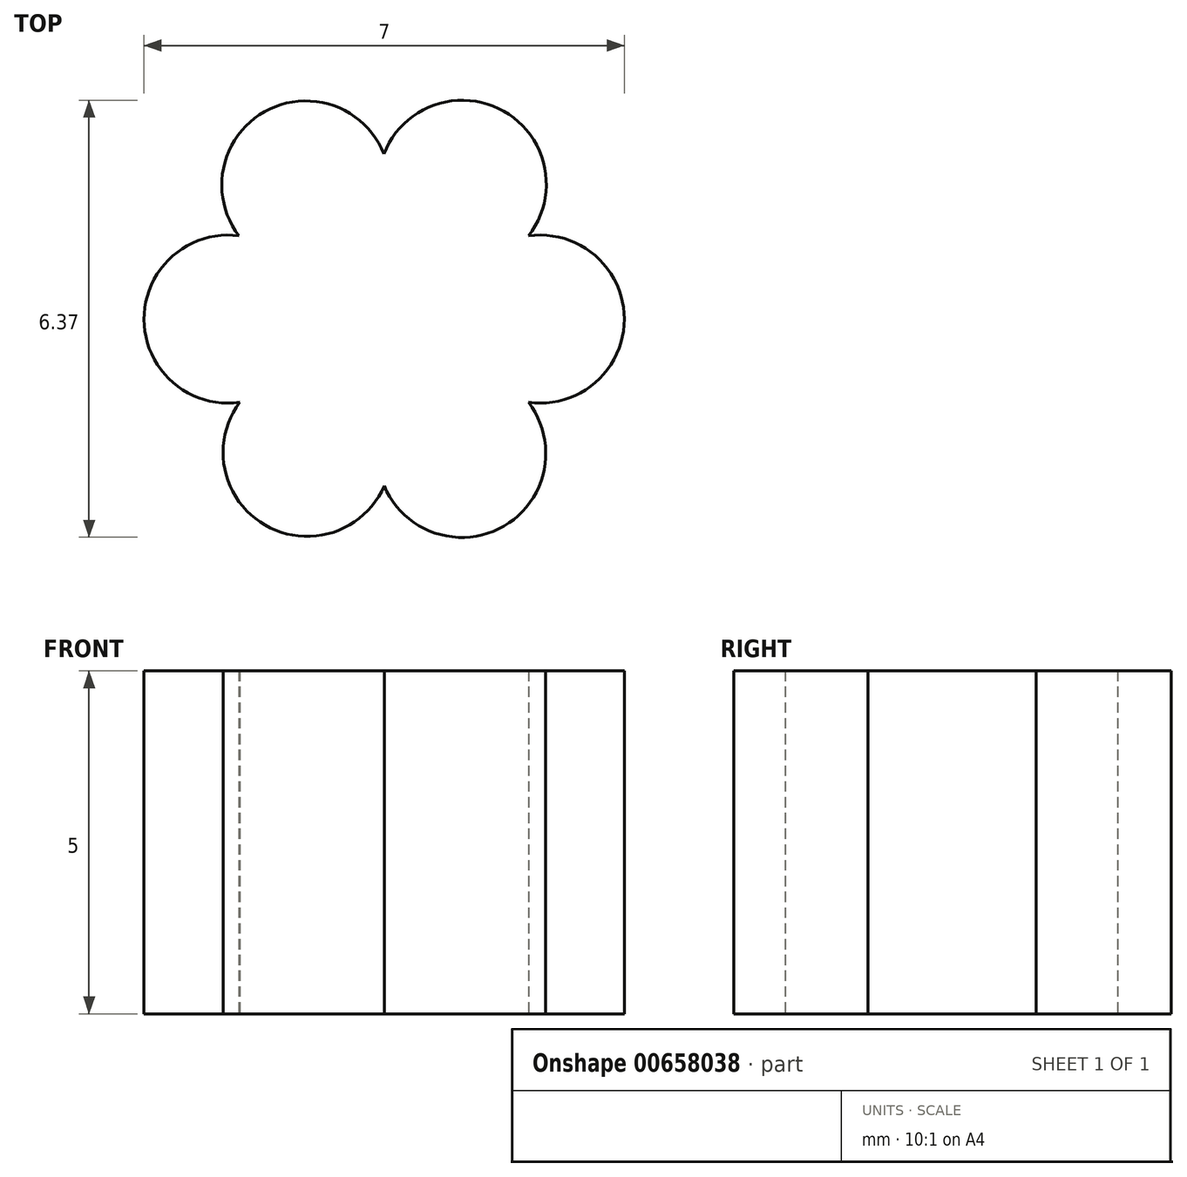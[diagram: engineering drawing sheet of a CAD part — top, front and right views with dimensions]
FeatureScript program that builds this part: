
annotation { "Feature Type Name" : "Feature", "Feature Type Description" : "" }
export const myFeature = defineFeature(function(context is Context, id is Id, definition is map)
    precondition{}
    {
        {
            var Q0;
            Q0=qCreatedBy(makeId("Top.planeOp"),FACE);
            var sketch = newSketch(context, id + "F0", { "sketchPlane" : qUnion([Q0])});
            skCircle(sketch, "E0", {"center": v(0, 0) * mm, "radius": 3.5 * mm});
            skCircle(sketch, "E1", {"center": v(-1.14, 1.96) * mm, "radius": 1.23 * mm});
            skCircle(sketch, "E2", {"center": v(-2.27, 0) * mm, "radius": 1.23 * mm});
            skCircle(sketch, "E3", {"center": v(-1.12, -1.94) * mm, "radius": 1.23 * mm});
            skCircle(sketch, "E4", {"center": v(1.13, -1.96) * mm, "radius": 1.23 * mm});
            skCircle(sketch, "E5", {"center": v(2.27, 0) * mm, "radius": 1.23 * mm});
            skCircle(sketch, "E6", {"center": v(1.14, 1.97) * mm, "radius": 1.23 * mm});
            skSolve(sketch);
        }
        {
            var Q0;
            {var subQ0=sQuery(id+"F0.wireOp",EDGE,"E2");var subQ1=sQuery(id+"F0.wireOp",EDGE,"E1");var subQ2=makeQuery(id+"F0.imprint","INTERSECT",VERTEX,{"disambiguationData":[OD(0.0)],"derivedFrom":[subQ1,subQ0]});Q0=makeQuery(id+"F0.imprint","IMPRINT",FACE,{"disambiguationData":[TD([[makeQuery(id+"F0.imprint","IMPRINT",EDGE,{"disambiguationData":[TD([[subQ2,1.0]])],"derivedFrom":subQ1}),1.0]])]});}
            var Q1;
            {var subQ0=sQuery(id+"F0.wireOp",EDGE,"E2");var subQ1=sQuery(id+"F0.wireOp",EDGE,"E1");var subQ6=makeQuery(id+"F0.imprint","INTERSECT",VERTEX,{"disambiguationData":[OD(0.0)],"derivedFrom":[subQ1,subQ0]});Q1=makeQuery(id+"F0.imprint","IMPRINT",FACE,{"disambiguationData":[TD([[makeQuery(id+"F0.imprint","IMPRINT",EDGE,{"disambiguationData":[TD([[subQ6,-1.0]])],"derivedFrom":subQ1}),-1.0]])]});}
            var Q2;
            {var subQ0=sQuery(id+"F0.wireOp",EDGE,"E2");var subQ1=sQuery(id+"F0.wireOp",EDGE,"E1");var subQ2=makeQuery(id+"F0.imprint","INTERSECT",VERTEX,{"disambiguationData":[OD(0.0)],"derivedFrom":[subQ1,subQ0]});Q2=makeQuery(id+"F0.imprint","IMPRINT",FACE,{"disambiguationData":[TD([[makeQuery(id+"F0.imprint","IMPRINT",EDGE,{"disambiguationData":[TD([[subQ2,-1.0]])],"derivedFrom":subQ1}),1.0]])]});}
            var Q3;
            {var subQ0=sQuery(id+"F0.wireOp",EDGE,"E3");var subQ1=sQuery(id+"F0.wireOp",EDGE,"E2");var subQ2=makeQuery(id+"F0.imprint","INTERSECT",VERTEX,{"disambiguationData":[OD(0.0)],"derivedFrom":[subQ1,subQ0]});Q3=makeQuery(id+"F0.imprint","IMPRINT",FACE,{"disambiguationData":[TD([[makeQuery(id+"F0.imprint","IMPRINT",EDGE,{"disambiguationData":[TD([[subQ2,-1.0]])],"derivedFrom":subQ1}),1.0]])]});}
            var Q4;
            {var subQ0=sQuery(id+"F0.wireOp",EDGE,"E3");var subQ1=sQuery(id+"F0.wireOp",EDGE,"E2");var subQ2=makeQuery(id+"F0.imprint","INTERSECT",VERTEX,{"disambiguationData":[OD(0.0)],"derivedFrom":[subQ1,subQ0]});Q4=makeQuery(id+"F0.imprint","IMPRINT",FACE,{"disambiguationData":[TD([[makeQuery(id+"F0.imprint","IMPRINT",EDGE,{"disambiguationData":[TD([[subQ2,-1.0]])],"derivedFrom":subQ1}),-1.0]])]});}
            var Q5;
            {var subQ0=sQuery(id+"F0.wireOp",EDGE,"E4");var subQ1=sQuery(id+"F0.wireOp",EDGE,"E3");var subQ2=makeQuery(id+"F0.imprint","INTERSECT",VERTEX,{"disambiguationData":[OD(0.0)],"derivedFrom":[subQ1,subQ0]});Q5=makeQuery(id+"F0.imprint","IMPRINT",FACE,{"disambiguationData":[TD([[makeQuery(id+"F0.imprint","IMPRINT",EDGE,{"disambiguationData":[TD([[subQ2,1.0]])],"derivedFrom":subQ1}),-1.0]])]});}
            var Q6;
            {var subQ0=sQuery(id+"F0.wireOp",EDGE,"E5");var subQ2=sQuery(id+"F0.wireOp",EDGE,"E4");var subQ4=makeQuery(id+"F0.imprint","INTERSECT",VERTEX,{"disambiguationData":[OD(0.0)],"derivedFrom":[subQ2,subQ0]});Q6=makeQuery(id+"F0.imprint","IMPRINT",FACE,{"disambiguationData":[TD([[makeQuery(id+"F0.imprint","IMPRINT",EDGE,{"disambiguationData":[TD([[subQ4,1.0]])],"derivedFrom":subQ2}),-1.0]])]});}
            var Q7;
            {var subQ0=sQuery(id+"F0.wireOp",EDGE,"E6");var subQ1=sQuery(id+"F0.wireOp",EDGE,"E1");var subQ2=makeQuery(id+"F0.imprint","INTERSECT",VERTEX,{"disambiguationData":[OD(0.0)],"derivedFrom":[subQ1,subQ0]});Q7=makeQuery(id+"F0.imprint","IMPRINT",FACE,{"disambiguationData":[TD([[makeQuery(id+"F0.imprint","IMPRINT",EDGE,{"disambiguationData":[TD([[subQ2,1.0]])],"derivedFrom":subQ1}),-1.0]])]});}
            var Q8;
            {var subQ0=sQuery(id+"F0.wireOp",EDGE,"E6");var subQ1=sQuery(id+"F0.wireOp",EDGE,"E1");var subQ2=makeQuery(id+"F0.imprint","INTERSECT",VERTEX,{"disambiguationData":[OD(0.0)],"derivedFrom":[subQ1,subQ0]});Q8=makeQuery(id+"F0.imprint","IMPRINT",FACE,{"disambiguationData":[TD([[makeQuery(id+"F0.imprint","IMPRINT",EDGE,{"disambiguationData":[TD([[subQ2,1.0]])],"derivedFrom":subQ1}),1.0]])]});}
            var Q9;
            {var subQ0=sQuery(id+"F0.wireOp",EDGE,"E6");var subQ1=sQuery(id+"F0.wireOp",EDGE,"E5");var subQ2=makeQuery(id+"F0.imprint","INTERSECT",VERTEX,{"disambiguationData":[OD(0.0)],"derivedFrom":[subQ1,subQ0]});Q9=makeQuery(id+"F0.imprint","IMPRINT",FACE,{"disambiguationData":[TD([[makeQuery(id+"F0.imprint","IMPRINT",EDGE,{"disambiguationData":[TD([[subQ2,-1.0]])],"derivedFrom":subQ1}),1.0]])]});}
            var Q10;
            {var subQ0=sQuery(id+"F0.wireOp",EDGE,"E5");var subQ1=sQuery(id+"F0.wireOp",EDGE,"E4");var subQ2=makeQuery(id+"F0.imprint","INTERSECT",VERTEX,{"disambiguationData":[OD(0.0)],"derivedFrom":[subQ1,subQ0]});Q10=makeQuery(id+"F0.imprint","IMPRINT",FACE,{"disambiguationData":[TD([[makeQuery(id+"F0.imprint","IMPRINT",EDGE,{"disambiguationData":[TD([[subQ2,1.0]])],"derivedFrom":subQ1}),1.0]])]});}
            var Q11;
            {var subQ0=sQuery(id+"F0.wireOp",EDGE,"E4");var subQ1=sQuery(id+"F0.wireOp",EDGE,"E3");var subQ2=makeQuery(id+"F0.imprint","INTERSECT",VERTEX,{"disambiguationData":[OD(0.0)],"derivedFrom":[subQ1,subQ0]});Q11=makeQuery(id+"F0.imprint","IMPRINT",FACE,{"disambiguationData":[TD([[makeQuery(id+"F0.imprint","IMPRINT",EDGE,{"disambiguationData":[TD([[subQ2,1.0]])],"derivedFrom":subQ1}),1.0]])]});}
            var Q12;
            {var subQ5=sQuery(id+"F0.wireOp",EDGE,"E2");var subQ7=sQuery(id+"F0.wireOp",EDGE,"E1");var subQ8=makeQuery(id+"F0.imprint","INTERSECT",VERTEX,{"disambiguationData":[OD(1.0)],"derivedFrom":[subQ7,subQ5]});Q12=makeQuery(id+"F0.imprint","IMPRINT",FACE,{"disambiguationData":[TD([[makeQuery(id+"F0.imprint","IMPRINT",EDGE,{"disambiguationData":[TD([[subQ8,-1.0]])],"derivedFrom":subQ7}),-1.0]])]});}
            extrude(context, id + "F1", {"entities" : qUnion([Q0, Q1, Q2, Q3, Q4, Q5, Q6, Q7, Q8, Q9, Q10, Q11, Q12]), "depth" : 5 * mm, "offsetDistance" : 25 * mm});
        }
    });
